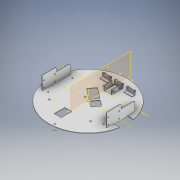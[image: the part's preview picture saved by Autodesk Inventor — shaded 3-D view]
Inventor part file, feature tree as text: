
AUTODESK INVENTOR PART (.ipt)
format: ipt  version: 2020 (Build 240168000, 168)  size: 748,032 bytes
history: native  units: mm
features: sketch x21, extrude x11, other x5, plane x3, fillet x1, projected_geometry x1
ambient origin geometry x8: Origin, YZ Plane, XZ Plane, XY Plane, X Axis, Y Axis, Z Axis, Center Point
bodies: Solid1 (feature_tree)
feature tree (42):
  other  "GornjaKonstrukcija_v.1.1.iam"
  other  "GonjaKonstrukcija_v.1.0.ipt:1"
  other  "5DržačaLidara.ipt:1"
  other  "5DržačaLidara.ipt:2"
  extrude  "Extrusion1"  Depth=3.0mm TaperAngle=0.0deg
  extrude  "Extrusion6"  Depth=2.0mm TaperAngle=0.0deg
  extrude  "Extrusion7"  Depth=1.0mm TaperAngle=0.0deg
  extrude  "Extrusion8"  Depth=1.0mm TaperAngle=0.0deg
  extrude  "Extrusion9"  Depth=1.0mm TaperAngle=0.0deg
  extrude  "Extrusion10"  Depth=1.0mm TaperAngle=0.0deg
  extrude  "Extrusion11"  Depth=2.0mm TaperAngle=0.0deg
  extrude  "Extrusion12"  [1 undecoded]
  extrude  "Extrusion13"  [1 undecoded]
  extrude  "Extrusion14"  [1 undecoded]
  fillet  "Fillet2"  [1 undecoded]
  extrude  "Extrusion15"  [1 undecoded]
  other  "Work Axis1"
  plane  "Work Plane1"
  plane  "Work Plane2"
  plane  "Work Plane3"
  sketch  "Sketch8"
  sketch  "Sketch8_1"  dims[d0=10.0mm d1=3.0mm d2=0.0mm]
  sketch  "Sketch8_2"  dims[d30=15.0mm d31=1.0mm d32=0.0mm]
  sketch  "Sketch8_3"  dims[d33=2.0mm d34=40.0mm d35=26.0mm d36=0.0mm d37=0.0mm]
  sketch  "Sketch8_4"
  sketch  "Sketch8_5"
  sketch  "Sketch8_1_1"  dims[d13=2.0mm d14=0.0mm d15=2.0mm d16=0.0mm]
  sketch  "Sketch8_2_1"  dims[d17=2.0mm d18=0.0mm d20=1.0mm d21=0.0mm]
  sketch  "Sketch8_3_1"  dims[d22=1.0mm d23=0.0mm d24=1.0mm d25=0.0mm]
  sketch  "Sketch8_4_1"  dims[d26=8.0mm d27=0.0mm d28=1.0mm d29=0.0mm]
  sketch  "Sketch12"
  sketch  "Sketch19"
  sketch  "Sketch20"
  sketch  "Sketch21"
  sketch  "Sketch22"
  sketch  "Sketch23"
  sketch  "Sketch24"
  projected_geometry  "Projected Loop1"
  sketch  "Sketch25"
  sketch  "Sketch26"
  sketch  "Sketch27"
  sketch  "Sketch28"
note: 5 required parameter values undecoded (feature->parameter linkage not recoverable at this tier; creation-order binding heuristic only, values carry confidence <= 0.55)
